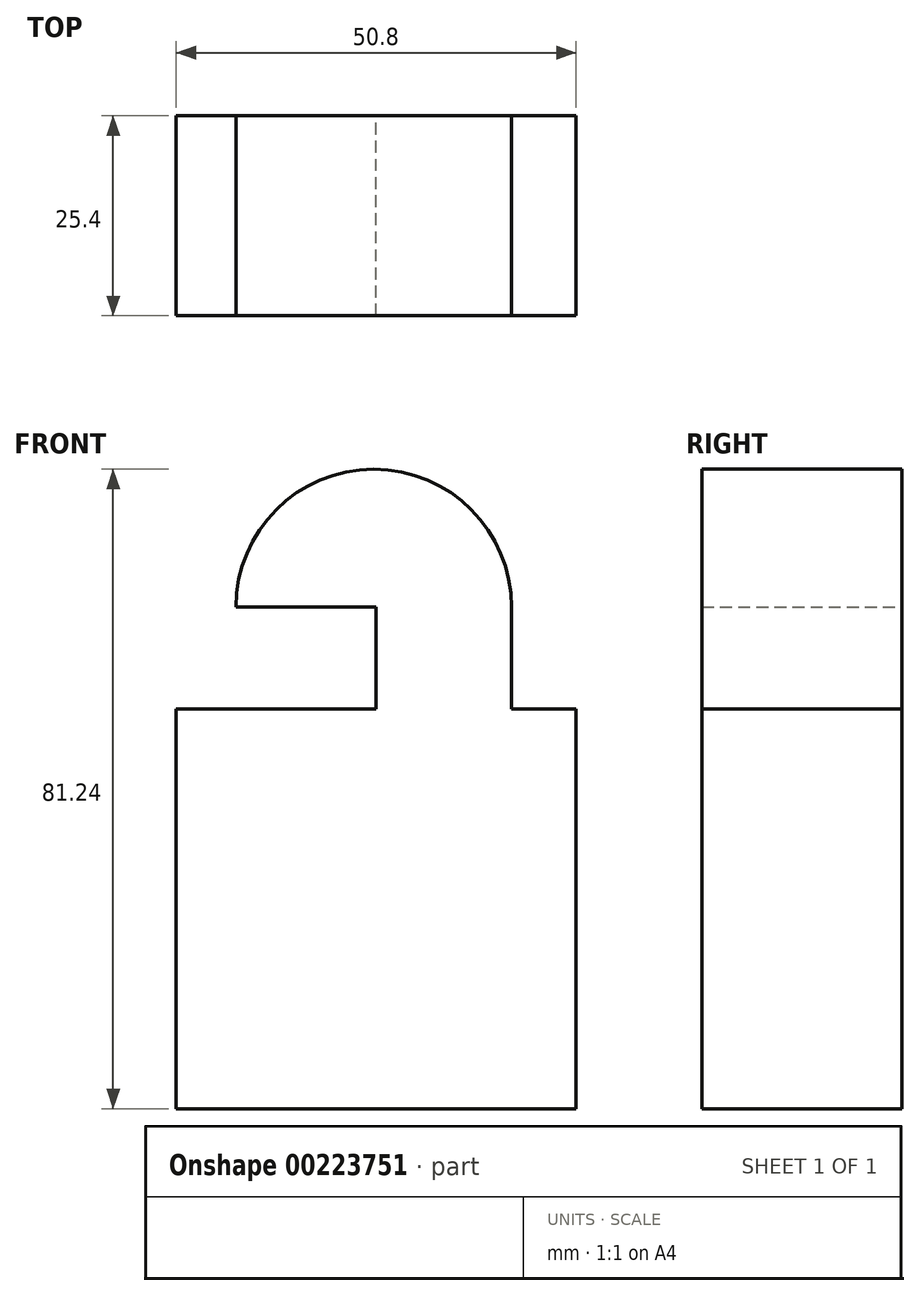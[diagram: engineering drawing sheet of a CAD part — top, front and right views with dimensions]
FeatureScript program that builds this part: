
annotation { "Feature Type Name" : "Feature", "Feature Type Description" : "" }
export const myFeature = defineFeature(function(context is Context, id is Id, definition is map)
    precondition{}
    {
        {
            var Q0;
            Q0=qCreatedBy(makeId("Front.planeOp"),FACE);
            var sketch = newSketch(context, id + "F0", { "sketchPlane" : qUnion([Q0])});
            skLineSegment(sketch, "E0.bottom", {"start": v(-25.4, -25.4) * mm, "end": v(25.4, -25.4) * mm});
            skLineSegment(sketch, "E0.top", {"start": v(-25.4, 25.4) * mm, "end": v(25.4, 25.4) * mm});
            skLineSegment(sketch, "E0.left", {"start": v(-25.4, -25.4) * mm, "end": v(-25.4, 25.4) * mm});
            skLineSegment(sketch, "E0.right", {"start": v(25.4, -25.4) * mm, "end": v(25.4, 25.4) * mm});
            skPoint(sketch, "E0.middle", {"position": v(0, 0) * mm});
            skLineSegment(sketch, "E1.bottom", {"start": v(-17.8, 25.4) * mm, "end": v(0, 25.4) * mm});
            skLineSegment(sketch, "E1.top", {"start": v(-17.8, 38.34) * mm, "end": v(0, 38.34) * mm});
            skLineSegment(sketch, "E1.left", {"start": v(-17.8, 25.4) * mm, "end": v(-17.8, 38.34) * mm});
            skLineSegment(sketch, "E1.right", {"start": v(0, 25.4) * mm, "end": v(0, 38.34) * mm});
            skLineSegment(sketch, "E2.bottom", {"start": v(0, 38.34) * mm, "end": v(17.2, 38.34) * mm});
            skLineSegment(sketch, "E2.top", {"start": v(0, 25.4) * mm, "end": v(17.2, 25.4) * mm});
            skLineSegment(sketch, "E2.left", {"start": v(0, 38.34) * mm, "end": v(0, 25.4) * mm});
            skLineSegment(sketch, "E2.right", {"start": v(17.2, 38.34) * mm, "end": v(17.2, 25.4) * mm});
            skArc(sketch, "E3", {"start": v(17.2, 38.34) * mm, "mid": v(-0.3, 55.84) * mm, "end": v(-17.8, 38.34) * mm});
            skSolve(sketch);
        }
        {
            var Q0;
            Q0=makeQuery(id+"F0.imprint","IMPRINT",FACE,{"disambiguationData":[TD([[makeQuery(id+"F0.imprint","IMPRINT",EDGE,{"derivedFrom":sQuery(id+"F0.wireOp",EDGE,"E1.top")}),1.0]])]});
            var Q1;
            Q1=makeQuery(id+"F0.imprint","IMPRINT",FACE,{"disambiguationData":[TD([[makeQuery(id+"F0.imprint","IMPRINT",EDGE,{"derivedFrom":sQuery(id+"F0.wireOp",EDGE,"E1.bottom")}),1.0]])]});
            var Q2;
            Q2=makeQuery(id+"F0.imprint","IMPRINT",FACE,{"disambiguationData":[TD([[makeQuery(id+"F0.imprint","IMPRINT",EDGE,{"derivedFrom":sQuery(id+"F0.wireOp",EDGE,"E0.bottom")}),1.0]])]});
            var Q3;
            Q3=makeQuery(id+"F0.imprint","IMPRINT",FACE,{"disambiguationData":[TD([[makeQuery(id+"F0.imprint","IMPRINT",EDGE,{"derivedFrom":sQuery(id+"F0.wireOp",EDGE,"E2.bottom")}),-1.0]])]});
            extrude(context, id + "F1", {"entities" : qUnion([Q0, Q1, Q2, Q3]), "depth" : 25.4 * mm});
        }
    });
